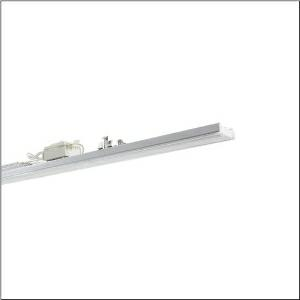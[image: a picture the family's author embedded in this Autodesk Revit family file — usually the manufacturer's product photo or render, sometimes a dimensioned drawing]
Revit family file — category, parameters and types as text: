
# Revit family: licross_11_recessed_mo_51te10mn4axg
name_source: partatom
category: Lighting Fixtures
units: mm (PartAtom-declared; Revit-internal decimal feet)

## family parameters
Cut with Voids When Loaded = No
Host = Face
Light Source = No
Part Type = Normal
Room Calculation Point = No
Round Connector Dimension = Use Diameter
Shared = No

## types (1)
- --- (1 x LED, 10000 lm, 55.2 W, 4000K)
    Apparent Load = 55 VA
    CIE Flux Codes = 50 81 96 100 100
    Color Rendering = 80
    Color Temperature = 4000K
    Default Elevation = 1800 mm
    Description = Licross 11 Recessed MO, luminaire insert, of sheet steel, galvanised, coil coated, white, length: 1.500mm, width: 66mm, height: 67mm, LED rated luminous flux: 10.000lm, light colour: 840, SDCM (Standard Deviation of Colour Matching)MacAdam ≤ 2 SDCM (initial), control gear: ON/OFF Multilumen, with plug, 3-pole, with phase selection, mains connection: 220..240V, AC, 50/60Hz, rated input power: 55W, internal wiring halogen-free, primary optical cover: cover, of PMMA, light emission: direct distribution, primary light characteristic: symmetric, protection rating (complete): IP54, insulation class (complete): insulation class I (protective earthing), certification: CE, ENEC, VDE, UKCA, protection symbol: D if used in an environment with non-conductive dust loads with corresponding accessories, impact resistance: IK06, permissible ambient temperature for indoor applications: -35..+40°C, corresponds to IFS (International Featured Standards) requirements for safety and quality in the food industry, reducing of maximum allowable ambient temperature of 5°C with ceiling mounting, The light source and the operating device comply with the requirements of the Ecodesign Regulation (EU) 2019/2020 and are replaceable in accordance with this regulation, packaging unit: 1 piece
    Height = 58 mm
    Lamp = 1 x LED
    Lamp Light Flux = 10000 lm
    Lamp Power = 55.2 W
    Lamp count = 1
    Length = 1500 mm
    Luminous efficacy = 181 lm/W
    Manufacturer = Siteco
    ModVariant = No
    Model = 51TE10MN4AXG
    Mounting Place = Ceiling
    Mounting Type = Pendant
    Number of Poles = 1
    OnlyDefault = Yes
    Power Factor = 1
    Product Name = Licross 11 Recessed MO
    Product group = luminaire insert | ceiling pendant
    ProductGroupID = 901
    Protection Class = Protection class I
    Protection Degree = IP 54
    RLX_Detail_Level = 1
    RLX_Emergency_Light_Flux = 0 lm
    RLX_Emergency_Type = 0
    RLX_Emergency_Type_DB = No
    RlxData = <blob elided: 22361 chars, md5=e56294c3>
    Socket = socket
    Standby Power = 0 W
    System Light Flux = 10000 lm
    System Power = 55 W
    Type Comments = factory setting: luminous flux: 100 % | (A | C | E) | 126 mA
    Type Image = l_1296930.jpg
    URL = http://relux.com
    VarID = @adj_089945
    Voltage = 0 V
    Weight = 0.00 kg
    Width = 66 mm

## geometry (parser evidence)
native form markers: Blend x4, Sweep x13
no freeform markers — native parametric forms only
